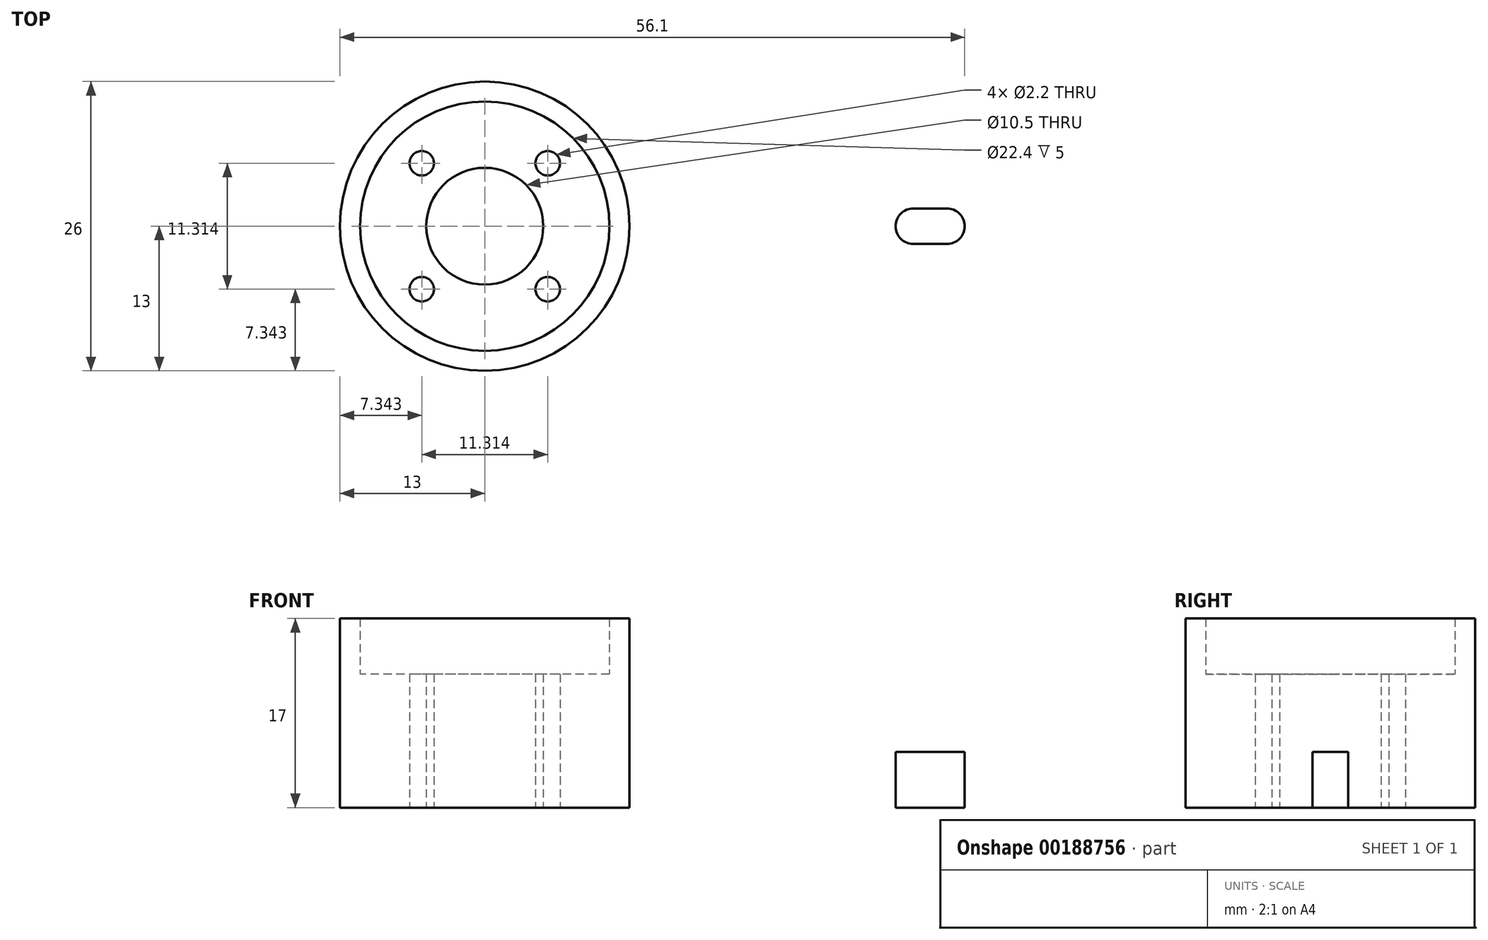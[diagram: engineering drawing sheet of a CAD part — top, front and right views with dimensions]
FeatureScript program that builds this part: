
annotation { "Feature Type Name" : "Feature", "Feature Type Description" : "" }
export const myFeature = defineFeature(function(context is Context, id is Id, definition is map)
    precondition{}
    {
        {
            var Q0;
            Q0=qCreatedBy(makeId("Top.planeOp"),FACE);
            var sketch = newSketch(context, id + "F0", { "sketchPlane" : qUnion([Q0])});
            skCircle(sketch, "E0", {"center": v(0, 0) * mm, "radius": 13 * mm});
            skLineSegment(sketch, "E1", {"start": v(0, 0) * mm, "end": v(40, 0) * mm, "construction": true});
            skPoint(sketch, "E2", {"position": v(40, 0) * mm});
            skLineSegment(sketch, "E3", {"start": v(38.5, 0) * mm, "end": v(41.5, 0) * mm, "construction": true});
            skArc(sketch, "E4.0.startCap", {"start": v(38.5, -1.6) * mm, "mid": v(36.9, 0) * mm, "end": v(38.5, 1.6) * mm});
            skArc(sketch, "E4.0.endCap", {"start": v(41.5, 1.6) * mm, "mid": v(43.1, 0) * mm, "end": v(41.5, -1.6) * mm});
            skLineSegment(sketch, "E4.0.left", {"start": v(38.5, 1.6) * mm, "end": v(41.5, 1.6) * mm});
            skLineSegment(sketch, "E4.0.right", {"start": v(38.5, -1.6) * mm, "end": v(41.5, -1.6) * mm});
            skLineSegment(sketch, "E5", {"start": v(11.53, 6) * mm, "end": v(11.53, -6) * mm, "construction": true});
            skLineSegment(sketch, "E6", {"start": v(41.5, 4.6) * mm, "end": v(41.5, -4.6) * mm, "construction": true});
            skArc(sketch, "E7", {"start": v(41.5, 4.6) * mm, "mid": v(46.1, 0) * mm, "end": v(41.5, -4.6) * mm});
            skLineSegment(sketch, "E8", {"start": v(11.53, 6) * mm, "end": v(41.5, 4.6) * mm});
            skLineSegment(sketch, "E9", {"start": v(11.53, -6) * mm, "end": v(41.5, -4.6) * mm});
            skCircle(sketch, "E10", {"center": v(0, 0) * mm, "radius": 5.25 * mm});
            skCircle(sketch, "E11", {"center": v(0, 0) * mm, "radius": 8 * mm, "construction": true});
            skCircle(sketch, "E12", {"center": v(5.66, 5.66) * mm, "radius": 1.1 * mm});
            skCircle(sketch, "E13", {"center": v(-5.66, 5.66) * mm, "radius": 1.1 * mm});
            skCircle(sketch, "E14", {"center": v(-5.66, -5.66) * mm, "radius": 1.1 * mm});
            skCircle(sketch, "E15", {"center": v(5.66, -5.66) * mm, "radius": 1.1 * mm});
            skLineSegment(sketch, "E16", {"start": v(5.66, 5.66) * mm, "end": v(-5.66, -5.66) * mm, "construction": true});
            skLineSegment(sketch, "E17", {"start": v(5.66, -5.66) * mm, "end": v(-5.66, 5.66) * mm, "construction": true});
            skSolve(sketch);
        }
        {
            var Q0;
            Q0=makeQuery(id+"F0.imprint","IMPRINT",FACE,{"disambiguationData":[TD([[makeQuery(id+"F0.imprint","IMPRINT",EDGE,{"derivedFrom":sQuery(id+"F0.wireOp",EDGE,"E10")}),-1.0]])]});
            extrude(context, id + "F1", {"entities" : qUnion([Q0]), "depth" : 12 * mm});
        }
        {
            var Q0;
            Q0=makeQuery(id+"F0.imprint","IMPRINT",FACE,{"disambiguationData":[TD([[makeQuery(id+"F0.imprint","IMPRINT",EDGE,{"derivedFrom":sQuery(id+"F0.wireOp",EDGE,"E4.0.startCap")}),1.0]])]});
            extrude(context, id + "F2", {"entities" : qUnion([Q0]), "operationType" : NewBodyOperationType.ADD, "depth" : 5 * mm});
        }
        {
            var Q0;
            Q0=makeQuery(id+"F1.opExtrude","CAP_FACE",FACE,{"disambiguationData":[OSD([sQuery(id+"F0.wireOp",EDGE,"E0"),sQuery(id+"F0.wireOp",EDGE,"E10")])],"isStart":false});
            var sketch = newSketch(context, id + "F3", { "sketchPlane" : qUnion([Q0])});
            skCircle(sketch, "E18", {"center": v(0, 0) * mm, "radius": 11.2 * mm});
            skSolve(sketch);
        }
        {
            var Q0;
            Q0=makeQuery(id+"F3.imprint","IMPRINT",FACE,{"disambiguationData":[TD([[makeQuery(id+"F3.imprint","IMPRINT",EDGE,{"derivedFrom":sQuery(id+"F3.wireOp",EDGE,"E18")}),-1.0]])]});
            extrude(context, id + "F4", {"entities" : qUnion([Q0]), "operationType" : NewBodyOperationType.ADD, "depth" : 5 * mm});
        }
    });
